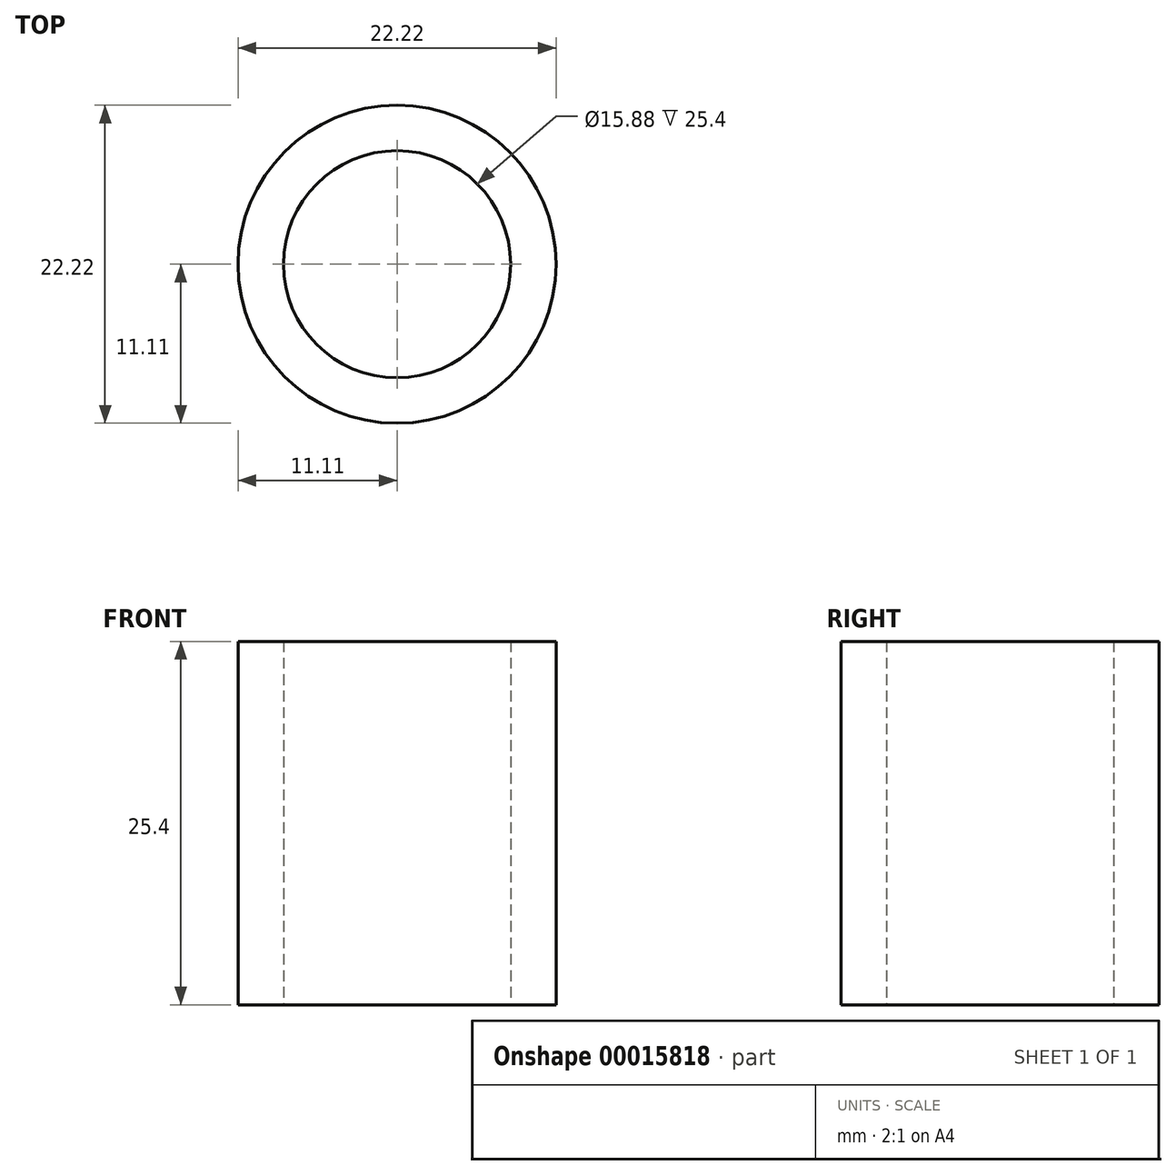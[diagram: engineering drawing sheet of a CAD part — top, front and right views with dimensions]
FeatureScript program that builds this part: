
annotation { "Feature Type Name" : "Feature", "Feature Type Description" : "" }
export const myFeature = defineFeature(function(context is Context, id is Id, definition is map)
    precondition{}
    {
        {
            var Q0;
            Q0=qCreatedBy(makeId("Top.planeOp"),FACE);
            var sketch = newSketch(context, id + "F0", { "sketchPlane" : qUnion([Q0])});
            skCircle(sketch, "E0", {"center": v(0, 0) * mm, "radius": 7.94 * mm});
            skCircle(sketch, "E1", {"center": v(0, 0) * mm, "radius": 11.11 * mm});
            skSolve(sketch);
        }
        {
            var Q0;
            Q0=qSketchRegion(id+"F0",true);
            extrude(context, id + "F1", {"entities" : qUnion([Q0]), "depth" : 25.4 * mm});
        }
    });
